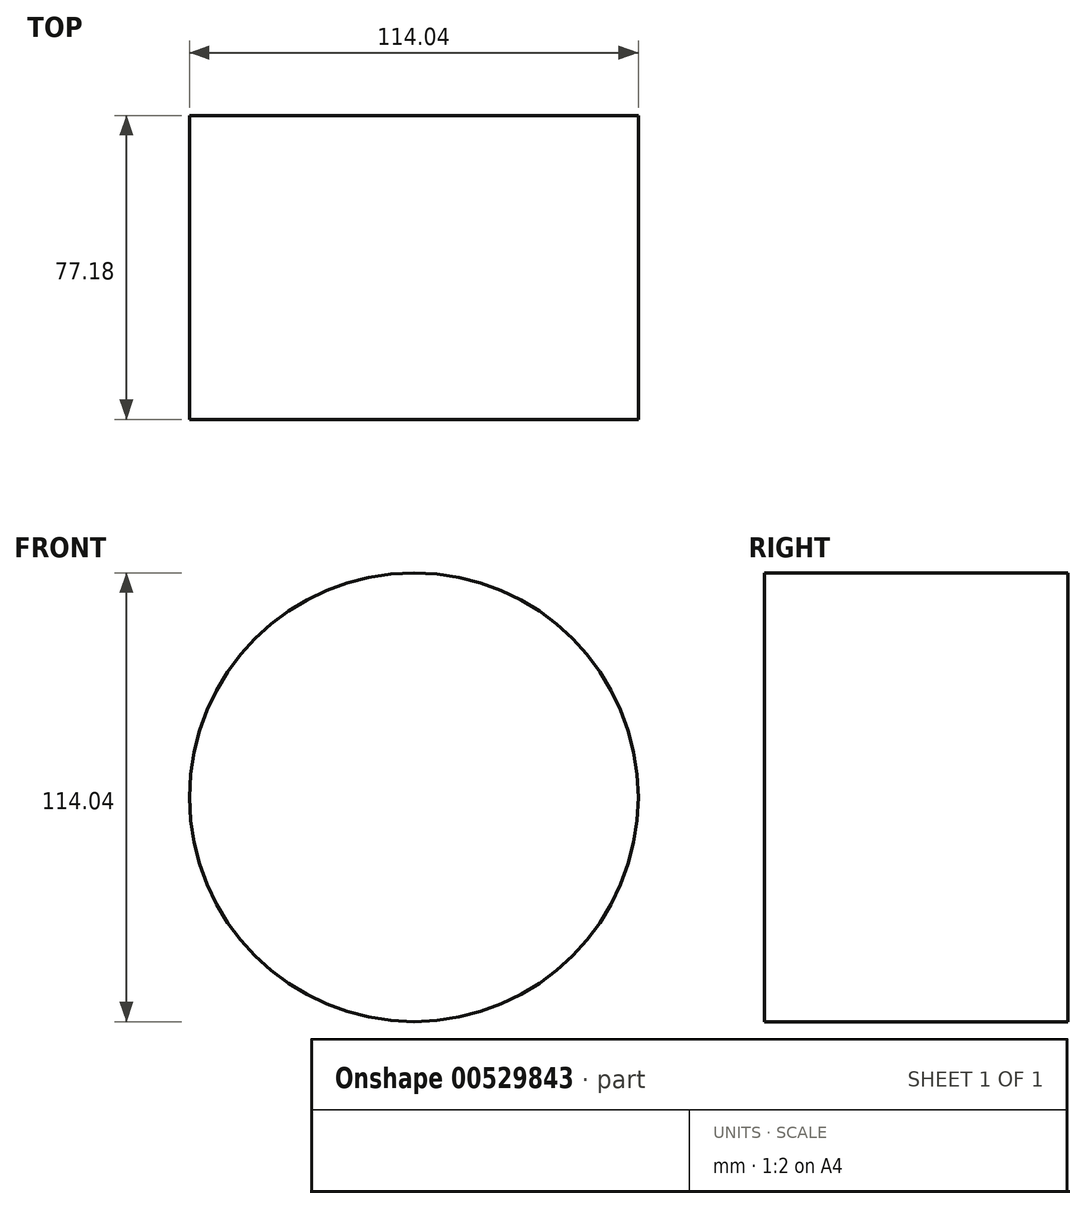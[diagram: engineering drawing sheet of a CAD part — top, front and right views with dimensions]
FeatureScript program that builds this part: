
annotation { "Feature Type Name" : "Feature", "Feature Type Description" : "" }
export const myFeature = defineFeature(function(context is Context, id is Id, definition is map)
    precondition{}
    {
        {
            var Q0;
            Q0=qCreatedBy(makeId("Front.planeOp"),FACE);
            var sketch = newSketch(context, id + "F0", { "sketchPlane" : qUnion([Q0])});
            skCircle(sketch, "E0", {"center": v(0, 0) * mm, "radius": 57.02 * mm});
            skSolve(sketch);
        }
        {
            var Q0;
            Q0=makeQuery(id+"F0.imprint","IMPRINT",FACE,{"disambiguationData":[TD([[makeQuery(id+"F0.imprint","IMPRINT",EDGE,{"derivedFrom":sQuery(id+"F0.wireOp",EDGE,"E0")}),1.0]])]});
            extrude(context, id + "F1", {"entities" : qUnion([Q0]), "depth" : 77.18 * mm, "offsetDistance" : 25.4 * mm});
        }
    });
